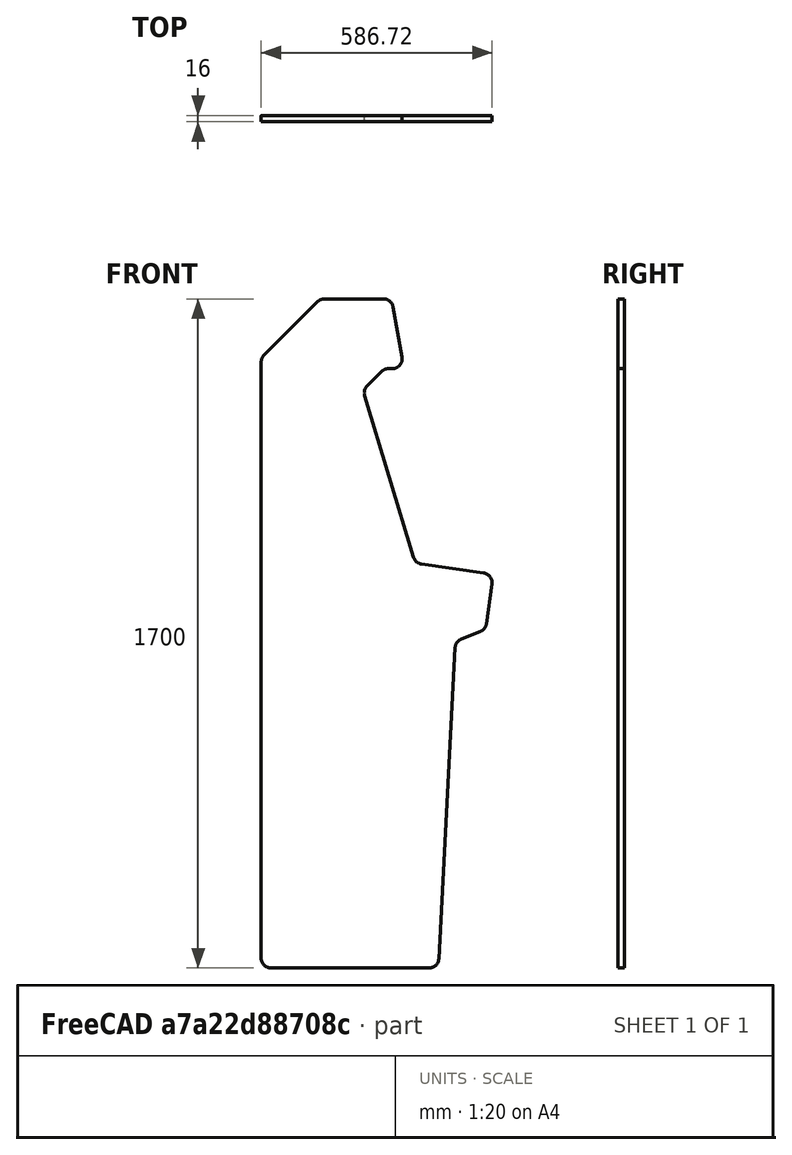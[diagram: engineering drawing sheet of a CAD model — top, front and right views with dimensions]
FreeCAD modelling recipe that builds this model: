
FCSTD DOCUMENT  (FreeCAD 1.0R39319 (Git))
Label: side
License: All rights reserved
LicenseURL: http://en.wikipedia.org/wiki/All_rights_reserved
objects: TechDraw::DrawViewDimension×5, PartDesign::Fillet×2, Sketcher::SketchObject×1, PartDesign::Pad×1, PartDesign::Body×1, TechDraw::DrawSVGTemplate×1, TechDraw::DrawViewPart×1, TechDraw::DrawPage×1
note: 12 computed .brp shape members not serialized (recipe doc carries the construction recipe); baked Part::Feature solids carry a one-line shape summary decoded from their .brp

FEATURE [Sketcher::SketchObject] Sketch  label="side_sketch"
  ArcFitTolerance = 0
  AttachmentSupport = -> [XZ_Plane]
  FullyConstrained = true
  MakeInternals = false
  MapMode = 5
  Placement = pos=(0,0,0) rot=(1,0,0;1.5708rad)
  sketch-geometry (14):
    g0: LineSegment StartX=0 StartY=0 StartZ=0 EndX=0 EndY=1550 EndZ=0
    g1: LineSegment StartX=0 StartY=0 StartZ=0 EndX=450 EndY=0 EndZ=0
    g2: LineSegment StartX=450 StartY=0 StartZ=0 EndX=493.498 EndY=830 EndZ=0
    g3: LineSegment StartX=570 StartY=860 StartZ=0 EndX=590 EndY=1000 EndZ=0
    g4: LineSegment StartX=590 StartY=1000 StartZ=0 EndX=392.01 EndY=1028.28 EndZ=0
    g5: LineSegment StartX=0 StartY=1550 StartZ=0 EndX=150 EndY=1700 EndZ=0
    g6: LineSegment StartX=150 StartY=1700 StartZ=0 EndX=331.508 EndY=1700 EndZ=0
    g7: LineSegment StartX=331.508 StartY=1700 StartZ=0 EndX=362.764 EndY=1522.73 EndZ=0
    g8: LineSegment [constr] StartX=590 StartY=1000 StartZ=0 EndX=0 EndY=1000 EndZ=0
    g9: LineSegment [constr] StartX=570 StartY=860 StartZ=0 EndX=0 EndY=860 EndZ=0
    g10: LineSegment StartX=493.498 StartY=830 StartZ=0 EndX=570 EndY=860 EndZ=0
    g11: LineSegment StartX=392.01 StartY=1028.28 StartZ=0 EndX=258.518 EndY=1468.49 EndZ=0
    g12: LineSegment StartX=362.764 StartY=1522.73 StartZ=0 EndX=312.764 EndY=1522.73 EndZ=0
    g13: LineSegment StartX=312.764 StartY=1522.73 StartZ=0 EndX=258.518 EndY=1468.49 EndZ=0
  constraints (41):
    c: Coincident(g1,g0)
    c: Horizontal(g1)
    c: Coincident(g2,g1)
    c: Coincident(g4,g3)
    c: Coincident(g5,g0)
    c: Coincident(g6,g5)
    c: Coincident(g7,g6)
    c: DistanceY(g1,g6) = 1700
    c: Coincident(g8,g3)
    c: PointOnObject(g8,g0)
    c: Horizontal(g8)
    c: DistanceX(g8,g8) = 590
    c: Coincident(g9,g3)
    c: PointOnObject(g9,g0)
    c: Horizontal(g9)
    c: DistanceX(g9,g9) = 570
    c: DistanceY(g3,g3) = 140
    c: DistanceY(g1,g3) = 1000
    c: Distance(g7) = 180
    c: Distance(g4) = 200
    c: Perpendicular(g3,g4)
    c: Angle(g2,g1) = 1.62316
    c: DistanceY(g2,g2) = 830
    c: Coincident(g0,g-1)
    c: DistanceX(g1,g1) = 450
    c: Coincident(g10,g2)
    c: Coincident(g10,g3)
    c: Coincident(g11,g4)
    c: Horizontal(g6)
    c: Vertical(g0)
    c: DistanceY(g0,g0) = 1550
    c: Angle(g4,g11) = 2.00713
    c: Angle(g6,g7) = 1.74533
    c: Coincident(g12,g7)
    c: Horizontal(g12)
    c: Coincident(g13,g11)
    c: Parallel(g13,g5)
    c: Coincident(g13,g12)
    c: DistanceX(g12,g12) = 50
    c: Distance(g11) = 460
    c: Angle(g0,g5) = 2.35619
FEATURE [PartDesign::Pad] Pad  label="side_pad"
  AllowMultiFace = false
  Direction = (0,-1,-1.035e-13)
  Length = 16
  Length2 = 100
  Placement = pos=(0,0,0) rot=(1,0,0;1.5708rad)
  Profile = -> Sketch
  Suppressed = false
  Type = 0
FEATURE [PartDesign::Fillet] Fillet  label="acute_fillet"
  Base = -> Pad [Edge17,Edge14,Edge11,Edge8,Edge5,Edge1,Edge29,Edge32]
  BaseFeature = -> Pad
  Placement = pos=(0,0,0) rot=(1,0,0;1.5708rad)
  Radius = 25
  Refine = true
  SupportTransform = false
  Suppressed = false
  UseAllEdges = false
FEATURE [PartDesign::Fillet] Fillet001  label="obtuse_fillet"
  Base = -> Fillet [Edge3,Edge52,Edge54,Edge56]
  BaseFeature = -> Fillet
  Placement = pos=(0,0,0) rot=(1,0,0;1.5708rad)
  Radius = 25
  Refine = true
  SupportTransform = false
  Suppressed = false
  UseAllEdges = false
FEATURE [PartDesign::Body] Body  label="side_body"
  AllowCompound = false
  Group = -> [Sketch,Pad,Fillet,Fillet001]
  Origin = -> Origin
  Tip = -> Fillet001
FEATURE [TechDraw::DrawSVGTemplate] Template
  Height = 1720
  Orientation = 0
  Width = 600
FEATURE [TechDraw::DrawViewPart] View
  CoarseView = false
  Direction = (0,1,0)
  Focus = 100
  HardHidden = false
  IsoCount = 0
  IsoHidden = false
  IsoVisible = false
  LockPosition = false
  Perspective = false
  Rotation = 0
  ScaleType = 0
  ScrubCount = 1
  SeamHidden = false
  SeamVisible = false
  SmoothHidden = false
  SmoothVisible = false
  Source = -> [Fillet001]
  X = 300
  XDirection = (-1,0,0)
  Y = 860
FEATURE [TechDraw::DrawViewDimension] Dimension
  AngleOverride = false
  Arbitrary = false
  ArbitraryTolerances = false
  EqualTolerance = false
  ExtensionAngle = 0
  FormatSpec = %.2f
  FormatSpecOverTolerance = %+.2w
  FormatSpecUnderTolerance = %+.2w
  Inverted = false
  LineAngle = 0
  LockPosition = false
  MeasureType = 1
  OverTolerance = 0
  References2D = -> [View]
  Rotation = 0
  ScaleType = 0
  TheoreticalExact = false
  Type = 1
  UnderTolerance = 0
  X = 130.405
  Y = -812.173
FEATURE [TechDraw::DrawViewDimension] Dimension002
  AngleOverride = false
  Arbitrary = false
  ArbitraryTolerances = false
  EqualTolerance = false
  ExtensionAngle = 0
  FormatSpec = %.2f
  FormatSpecOverTolerance = %+.2w
  FormatSpecUnderTolerance = %+.2w
  Inverted = false
  LineAngle = 0
  LockPosition = false
  MeasureType = 1
  OverTolerance = 0
  References2D = -> [View]
  Rotation = 0
  ScaleType = 0
  TheoreticalExact = false
  Type = 0
  UnderTolerance = 0
  X = -219.017
  Y = -325.499
FEATURE [TechDraw::DrawViewDimension] Dimension003
  AngleOverride = false
  Arbitrary = false
  ArbitraryTolerances = false
  EqualTolerance = false
  ExtensionAngle = 0
  FormatSpec = %.2f
  FormatSpecOverTolerance = %+.2w
  FormatSpecUnderTolerance = %+.2w
  Inverted = false
  LineAngle = 0
  LockPosition = false
  MeasureType = 1
  OverTolerance = 0
  References2D = -> [View]
  Rotation = 0
  ScaleType = 0
  TheoreticalExact = false
  Type = 0
  UnderTolerance = 0
  X = -66.9516
  Y = 0
FEATURE [TechDraw::DrawViewDimension] Dimension004
  AngleOverride = false
  Arbitrary = false
  ArbitraryTolerances = false
  EqualTolerance = false
  ExtensionAngle = 0
  FormatSpec = %.2f
  FormatSpecOverTolerance = %+.2w
  FormatSpecUnderTolerance = %+.2w
  Inverted = false
  LineAngle = 0
  LockPosition = false
  MeasureType = 1
  OverTolerance = 0
  References2D = -> [View]
  Rotation = 0
  ScaleType = 0
  TheoreticalExact = false
  Type = 2
  UnderTolerance = 0
  X = 230.057
  Y = 7.83477
FEATURE [TechDraw::DrawViewDimension] Dimension005
  AngleOverride = false
  Arbitrary = false
  ArbitraryTolerances = false
  EqualTolerance = false
  ExtensionAngle = 0
  FormatSpec = %.2f
  FormatSpecOverTolerance = %+.2w
  FormatSpecUnderTolerance = %+.2w
  Inverted = false
  LineAngle = 0
  LockPosition = false
  MeasureType = 1
  OverTolerance = 0
  References2D = -> [View]
  Rotation = 0
  ScaleType = 0
  TheoreticalExact = false
  Type = 1
  UnderTolerance = 0
  X = 78.7038
  Y = 765.314
FEATURE [TechDraw::DrawPage] Page
  KeepUpdated = true
  NextBalloonIndex = 1
  ProjectionType = 0
  Template = -> Template
  Views = -> [View,Dimension,Dimension002,Dimension003,Dimension004,Dimension005]
